# Revit family: 7428 Bloc ETL
name_source: partatom
category: Lighting Fixtures
revit_build: Autodesk Revit 2018 (Build: 20170223_1515(x64)
units: mm (PartAtom-declared; Revit-internal decimal feet)

## family parameters
Always vertical = Yes
Cut with Voids When Loaded = No
Host = Wall
Light Source = Yes
OmniClass Number = 23.80.70.00
OmniClass Title = Lighting
Part Type = Normal
Room Calculation Point = No
Round Connector Dimension = Use Diameter
Shared = No

## types (2) — shared parameters
Color Filter = 16777215
Dimmable = No
Dimming Lamp Color Temperature Shift = <None>
Lamp = LED
Light Source Fixed = Yes
Main Finish = Polished Chrome
Main Material = Metal - Zinc
Manufacturer = Astro Lighting Ltd
Tilt Angle = 90.00°
URL = www.astrolighting.com

## per-type parameters (varying)
| type | ADA compliant | Apparent Load | Driver Included | Driver Required | Efficacy (lm/w) | Electrical Class | Location rating | Photometric Web File | Power (Watts) | Product Code | Product Location | Product Name | Product SKU | Wattage Comments |
| CE |  | 6 VA | Yes (Integral) | No | 36.45 | 1 | IP20 | generic | 2.5 | 659 | Indoor | Fosso Switched | 1138005 |  |
| ETL | Yes | 7 VA | No | Constant Current 350mA | 27.94 | 2 | DAMP | GNC-20541 7428 Bloc LED IES.ies | 3.4 | 7428 | Bathroom / Indoor | Bloc | 1146008 | Measured value taken from Goniophotometer test using Self SLT3-350ISC driver. |

## geometry (parser evidence)
native form markers: Sweep x1
no freeform markers — native parametric forms only
